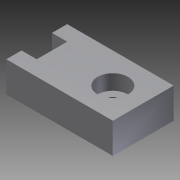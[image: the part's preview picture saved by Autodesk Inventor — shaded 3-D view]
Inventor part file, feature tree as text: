
AUTODESK INVENTOR PART (.ipt)
format: ipt  version: 2011 SP1 (Build 150282100, 282)  size: 97,280 bytes
history: native  units: mm
features: extrude x2, sketch x2
ambient origin geometry x8: Origin, YZ Plane, XZ Plane, XY Plane, X Axis, Y Axis, Z Axis, Center Point
bodies: Solid1 (feature_tree)
feature tree (4):
  extrude  "Extrusion1"  Depth=10.0mm
  extrude  "Extrusion2"  Depth=5.0mm
  sketch  "Sketch1"  dims[d0=5.0mm d1=10.0mm]
  sketch  "Sketch2"  dims[d2=5.0mm d3=5.0mm d4=5.0mm d5=35.0mm d7=10.0mm d8=5.0mm d9=10.0mm d10=0.0mm d11=10.0mm d12=5.0mm d13=0.0mm]
